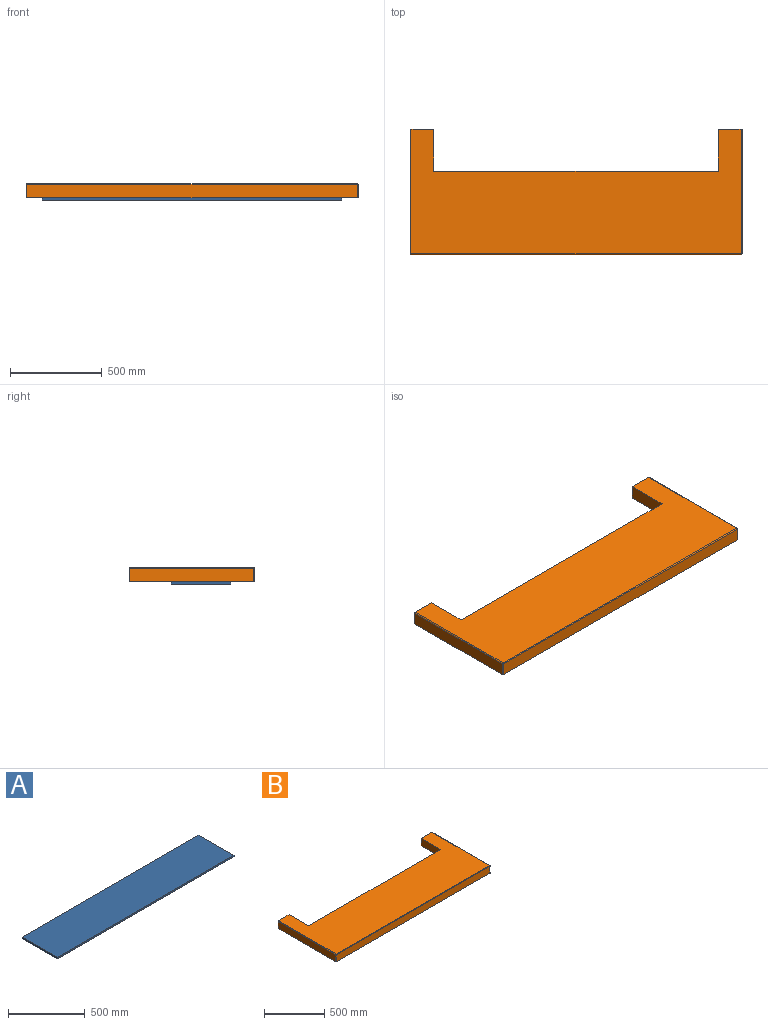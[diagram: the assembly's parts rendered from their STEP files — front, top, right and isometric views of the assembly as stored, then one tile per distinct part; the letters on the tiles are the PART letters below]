
ASSEMBLY  parts=2 mates=1
PART A: 6 faces, bbox 1632x323.9x12.7 mm
  f0: plane 1631.95x12.7mm, normal (0,-1,0), area 20725.8mm2, adj f1,f3,f4,f5
  f1: plane 323.85x12.7mm, normal (1,0,0), area 4112.9mm2, adj f0,f2,f4,f5
  f2: plane 1631.95x12.7mm, normal (0,1,0), area 20725.8mm2, adj f1,f3,f4,f5
  f3: plane 323.85x12.7mm, normal (-1,0,0), area 4112.9mm2, adj f0,f2,f4,f5
  f4: plane 1631.95x323.85mm, normal (0,0,1), area 528507mm2, adj f0,f1,f2,f3
  f5: plane 1631.95x323.85mm, normal (0,0,-1), area 528507mm2, adj f0,f1,f2,f3
PART B: 17 faces, bbox 1809.8x682.6x76.2 mm
  f0: plane 677.55x71.12mm, normal (1,0,0), area 48187mm2, adj f1,f9,f10,f11
  f1: plane 130.18x76.2mm, normal (0,1,0), area 9913.8mm2, adj f0,f2,f8,f9,f10
  f2: plane 228.6x76.2mm, normal (-1,0,0), area 17419.3mm2, adj f1,f3,f8,f9
  f3: plane 1549.4x76.2mm, normal (0,1,0), area 118064.3mm2, adj f2,f4,f8,f9
  f4: plane 228.6x76.2mm, normal (1,0,0), area 17419.3mm2, adj f3,f5,f8,f9
  f5: plane 130.18x76.2mm, normal (0,1,0), area 9913.8mm2, adj f4,f6,f8,f9,f13
  f6: plane 677.55x71.12mm, normal (-1,0,0), area 48187mm2, adj f5,f9,f13,f16
  f7: plane 1799.59x71.12mm, normal (0,-1,0), area 127986.8mm2, adj f9,f11,f14,f16
  f8: plane 1799.59x677.55mm, normal (0,0,1), area 865110.4mm2, adj f1,f2,f3,f4,f5,f10,f13,f14
  f9: plane 1809.75x682.63mm, normal (0,0,-1), area 881176.7mm2, adj f0,f1,f2,f3,f4,f5,f6,f7
  f10: cylinder r=5.08mm len=677.55mm, axis (0,-1,0), area 5406.6mm2, adj f0,f1,f8,f12
  f11: cylinder r=5.08mm len=71.12mm, axis (0,0,-1), area 567.5mm2, adj f0,f7,f9,f12
  f12: sphere r=5.08mm, area 40.5mm2, adj f10,f11,f14
  f13: cylinder r=5.08mm len=677.55mm, axis (0,1,0), area 5406.6mm2, adj f5,f6,f8,f15
  f14: cylinder r=5.08mm len=1799.59mm, axis (-1,0,0), area 14360.1mm2, adj f7,f8,f12,f15
  f15: sphere r=5.08mm, area 40.5mm2, adj f13,f14,f16
  f16: cylinder r=5.08mm len=71.12mm, axis (0,0,-1), area 567.5mm2, adj f6,f7,f9,f15
PLACE A t=(160.5,-401.46,202.01)mm
PLACE B t=(249.4,-77.61,214.71)mm
MATE fastened B.f9 <-> A.f4  axis (0,0,-1) through (-655.48,-77.61,214.71)mm
